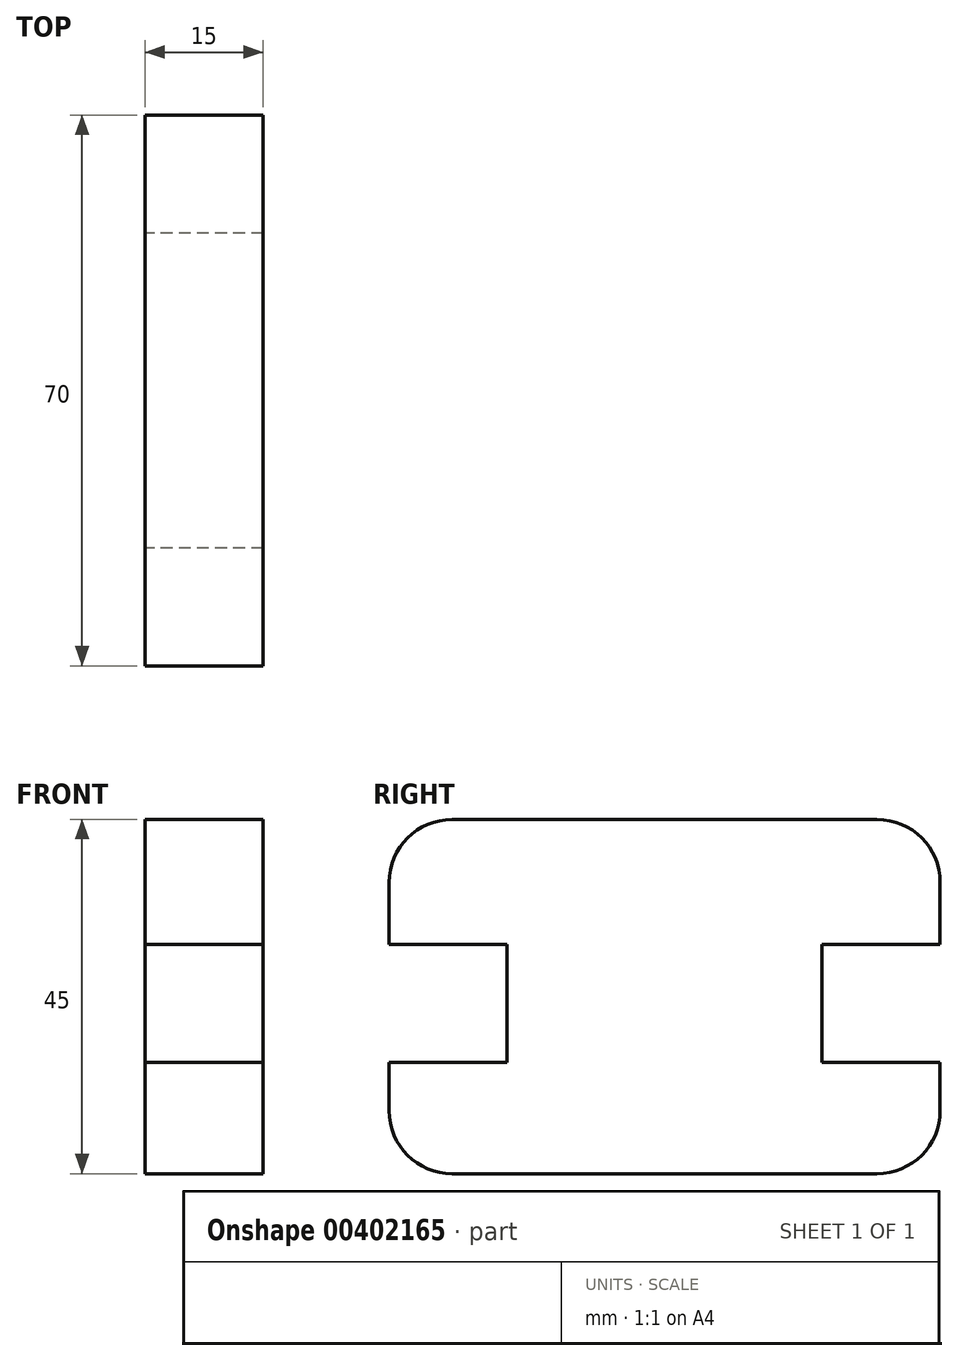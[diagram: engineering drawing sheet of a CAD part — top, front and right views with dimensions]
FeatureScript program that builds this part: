
annotation { "Feature Type Name" : "Feature", "Feature Type Description" : "" }
export const myFeature = defineFeature(function(context is Context, id is Id, definition is map)
    precondition{}
    {
        {
            var Q0;
            Q0=qCreatedBy(makeId("Right.planeOp"),FACE);
            var sketch = newSketch(context, id + "F0", { "sketchPlane" : qUnion([Q0])});
            skLineSegment(sketch, "E0.bottom", {"start": v(27, 22.5) * mm, "end": v(-27, 22.5) * mm});
            skLineSegment(sketch, "E0.top", {"start": v(27, -22.5) * mm, "end": v(-27, -22.5) * mm});
            skLineSegment(sketch, "E0.left", {"start": v(35, 14.5) * mm, "end": v(35, 6.62) * mm});
            skLineSegment(sketch, "E0.right", {"start": v(-35, 14.5) * mm, "end": v(-35, 6.62) * mm});
            skPoint(sketch, "E1.visualSharp", {"position": v(35, 22.5) * mm});
            skArc(sketch, "E1.filletArc", {"start": v(35, 14.5) * mm, "mid": v(32.66, 20.16) * mm, "end": v(27, 22.5) * mm});
            skPoint(sketch, "E2.visualSharp", {"position": v(-35, 22.5) * mm});
            skArc(sketch, "E2.filletArc", {"start": v(-27, 22.5) * mm, "mid": v(-32.66, 20.16) * mm, "end": v(-35, 14.5) * mm});
            skPoint(sketch, "E3.visualSharp", {"position": v(35, -22.5) * mm});
            skArc(sketch, "E3.filletArc", {"start": v(27, -22.5) * mm, "mid": v(32.66, -20.16) * mm, "end": v(35, -14.5) * mm});
            skPoint(sketch, "E4.visualSharp", {"position": v(-35, -22.5) * mm});
            skArc(sketch, "E4.filletArc", {"start": v(-35, -14.5) * mm, "mid": v(-32.66, -20.16) * mm, "end": v(-27, -22.5) * mm});
            skLineSegment(sketch, "E5", {"start": v(35, 6.62) * mm, "end": v(20, 6.62) * mm});
            skLineSegment(sketch, "E6", {"start": v(20, 6.62) * mm, "end": v(20, -8.38) * mm});
            skLineSegment(sketch, "E7", {"start": v(20, -8.38) * mm, "end": v(35, -8.38) * mm});
            skLineSegment(sketch, "E8", {"start": v(-35, -8.38) * mm, "end": v(-20, -8.38) * mm});
            skLineSegment(sketch, "E9", {"start": v(-20, -8.38) * mm, "end": v(-20, 6.62) * mm});
            skLineSegment(sketch, "E10", {"start": v(-20, 6.62) * mm, "end": v(-35, 6.62) * mm});
            skLineSegment(sketch, "E11.trimOffspring", {"start": v(-35, -8.38) * mm, "end": v(-35, -14.5) * mm});
            skLineSegment(sketch, "E12.trimOffspring", {"start": v(35, -8.38) * mm, "end": v(35, -14.5) * mm});
            skSolve(sketch);
        }
        {
            var Q0;
            Q0 = qSketchRegion(id + "F0", true);
            extrude(context, id + "F1", {"entities" : qUnion([Q0]), "depth" : 15 * mm});
        }
    });
